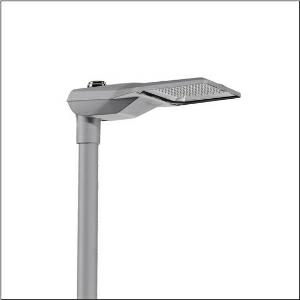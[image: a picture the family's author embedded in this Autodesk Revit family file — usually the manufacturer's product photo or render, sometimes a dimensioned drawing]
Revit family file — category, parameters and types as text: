
# Revit family: streetlight_sl_21_midi___stw1_0a_5xe7e37n08nb_3567
name_source: partatom
category: Lighting Fixtures
units: mm (PartAtom-declared; Revit-internal decimal feet)

## family parameters
Cut with Voids When Loaded = No
Host = Face
Light Source = No
Part Type = Normal
Room Calculation Point = No
Round Connector Dimension = Use Diameter
Shared = No

## types (1)
- --- (1 x LED, 22700 lm, 151.2 W, 3000K)
    Apparent Load = 151 VA
    CIE Flux Codes = 39 75 98 100 100
    Color Rendering = 70
    Color Temperature = 3000K
    Default Elevation = 1800 mm
    Description = Streetlight SL 21 midi, mast luminaire, primary light control with lens, of PMMA, primary optical cover: cover, of toughened safety glass, transparent, light distribution: STW1.0a, light emission: direct distribution, primary light characteristic: asymmetric, installation type: side-entry, LED, 3G 2.5mm², High Power LED, rated luminous flux: 22.700lm, luminous efficacy: 150lm/W, light colour: 730, colour temperature: 3000K, control gear: NEMA (7pin), control: overheat protection, pre-setting: linear dimming characteristic, constant luminous flux control, time-dependent luminous flux control, flexible luminous flux parameterisation, mains connection: 220..240V, AC, 50/60Hz, connection cable pre-assembled, cable length: 12,5m, wiring characteristics: H05VV-F, start of lifetime: 151W, end of service life: 157W, reduction: 70W, luminaire housing, of diecast aluminium (EN AC-44300), powder-coated, Siteco® metallic grey (DB 702S), corrosivity category C5 mid according to DIN EN ISO 12944, multi-level sealing system, sealing non-destructively replaceable, inclination adjustable: 0°, 5°, 10°, 15°, length: 644mm, width: 335mm, height: 110mm, spigot size: 42mm (side-entry), mounting height: 4..8m, protection rating (complete): IP66, insulation class (complete): insulation class I (protective earthing), certification: CE, ENEC, ENEC+, VDE, impact resistance: IK10, permissible operating ambient temperature for outdoor applications: -40..+50°C, standard-compliant lighting for roads and squares, packaging unit: 1 piece

Light Distribution: STW1.0a
    Height = 111 mm
    Lamp = 1 x LED
    Lamp Light Flux = 22700 lm
    Lamp Power = 151.2 W
    Lamp count = 1
    Length = 644 mm
    Luminous efficacy = 150 lm/W
    Manufacturer = Siteco
    ModVariant = No
    Model = 5XE7E37N08NB
    Number of Poles = 1
    OnlyDefault = Yes
    Power Factor = 1
    Product Name = Streetlight SL 21 midi | STW1.0a
    Product group = mast luminaire | pylon top
    ProductGroupID = 6100
    Protection Class = Protection class I
    Protection Degree = IP 66
    RLX_Detail_Level = 1
    RLX_Emergency_Light_Flux = 0 lm
    RLX_Emergency_Type = 0
    RLX_Emergency_Type_DB = No
    RlxData = <blob elided: 26653 chars, md5=c12749a4>
    Socket = socket
    Standby Power = 0 W
    System Light Flux = 22700 lm
    System Power = 151 W
    Type Comments = factory setting: luminous flux: 100 % | dim-lin: 254 | 802 mA
    Type Image = l_1294377.jpg
    URL = http://relux.com
    VarID = @adj_134934
    Voltage = 0 V
    Weight = 0.00 kg
    Width = 336 mm

## geometry (parser evidence)
native form markers: Blend x4, Sweep x10
no freeform markers — native parametric forms only
